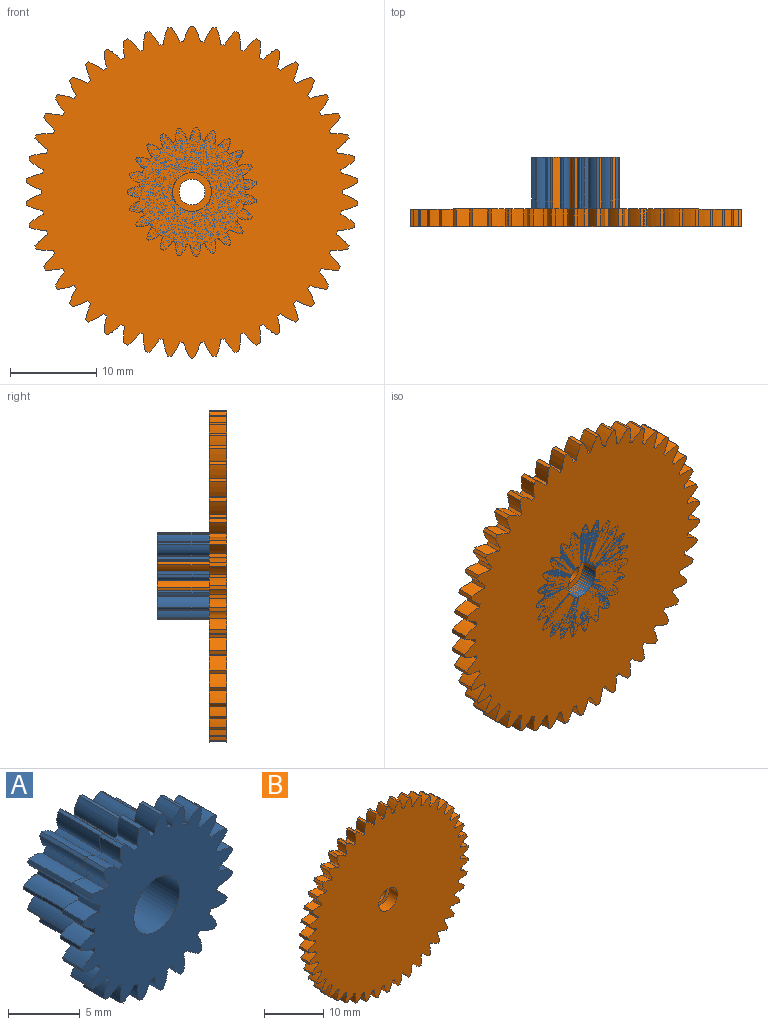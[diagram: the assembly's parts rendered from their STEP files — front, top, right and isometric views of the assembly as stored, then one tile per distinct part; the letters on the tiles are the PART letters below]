
ASSEMBLY  parts=2 mates=1
PART A: 156 faces, bbox 15x8x15 mm
  f0: cylinder r=5.1mm len=6mm, axis (0,-1,0), area 1.7mm2, adj f15,f56,f61,f86
  f1: cylinder r=5.1mm len=6mm, axis (0,-1,0), area 1.7mm2, adj f15,f50,f58,f86
  f2: cylinder r=5.1mm len=6mm, axis (0,-1,0), area 1.7mm2, adj f15,f17,f55,f86
  f3: cylinder r=5.1mm len=6mm, axis (0,-1,0), area 1.7mm2, adj f15,f52,f53,f86
  f4: cylinder r=5.1mm len=6mm, axis (0,-1,0), area 1.7mm2, adj f15,f44,f49,f86
  f5: cylinder r=5.1mm len=6mm, axis (0,-1,0), area 1.7mm2, adj f15,f46,f59,f86
  f6: cylinder r=5.1mm len=6mm, axis (0,-1,0), area 1.7mm2, adj f15,f43,f47,f86
  f7: cylinder r=5.1mm len=6mm, axis (0,-1,0), area 1.7mm2, adj f15,f40,f41,f86
  f8: cylinder r=5.1mm len=6mm, axis (0,-1,0), area 1.7mm2, adj f15,f29,f37,f86
  f9: cylinder r=5.1mm len=6mm, axis (0,-1,0), area 1.7mm2, adj f15,f34,f35,f86
  f10: cylinder r=5.1mm len=6mm, axis (0,-1,0), area 1.7mm2, adj f15,f26,f31,f86
  f11: cylinder r=5.1mm len=6mm, axis (0,-1,0), area 1.7mm2, adj f15,f20,f28,f86
  f12: cylinder r=5.1mm len=6mm, axis (0,-1,0), area 1.7mm2, adj f15,f25,f38,f86
  f13: cylinder r=5.1mm len=6mm, axis (0,-1,0), area 1.7mm2, adj f15,f22,f23,f86
  f14: cylinder r=5.1mm len=6mm, axis (0,-1,0), area 1.7mm2, adj f15,f19,f32,f86
  f15: plane 10.19x10.14mm, normal (0,1,0), area 46mm2, adj f0,f1,f2,f3,f4,f5,f6,f7
  f16: cylinder r=2.25mm len=8mm, axis (0,-1,0), area 113.1mm2, adj f15,f85
  f17: extruded ~6x1.28mm, area 8.8mm2, adj f2,f15,f18,f86
  f18: cylinder r=3.75mm len=6mm, axis (0,-1,0), area 3.4mm2, adj f15,f17,f19,f86
  f19: extruded ~6x1.28mm, area 8.8mm2, adj f14,f15,f18,f86
  f20: extruded ~6x1.43mm, area 8.8mm2, adj f11,f15,f21,f86
  f21: cylinder r=3.75mm len=6mm, axis (0,-1,0), area 3.4mm2, adj f15,f20,f22,f86
  f22: extruded ~6x1.19mm, area 8.8mm2, adj f13,f15,f21,f86
  f23: extruded ~6x1.27mm, area 8.8mm2, adj f13,f15,f24,f86
  f24: cylinder r=3.75mm len=6mm, axis (0,-1,0), area 3.4mm2, adj f15,f23,f25,f86
  f25: extruded ~6x1.41mm, area 8.8mm2, adj f12,f15,f24,f86
  f26: extruded ~6x1.34mm, area 8.8mm2, adj f10,f15,f27,f86
  f27: cylinder r=3.75mm len=6mm, axis (0,-1,0), area 3.4mm2, adj f15,f26,f28,f86
  f28: extruded ~6x1.2mm, area 8.8mm2, adj f11,f15,f27,f86
  f29: extruded ~6x1.02mm, area 8.8mm2, adj f8,f15,f30,f86
  f30: cylinder r=3.75mm len=6mm, axis (0,-1,0), area 3.4mm2, adj f15,f29,f31,f86
  f31: extruded ~6x1.41mm, area 8.8mm2, adj f10,f15,f30,f86
  f32: extruded ~6x1.43mm, area 8.8mm2, adj f14,f15,f33,f86
  f33: cylinder r=3.75mm len=6mm, axis (0,-1,0), area 3.4mm2, adj f15,f32,f34,f86
  f34: extruded ~6x1.1mm, area 8.8mm2, adj f9,f15,f33,f86
  f35: extruded ~6x1.33mm, area 8.8mm2, adj f9,f15,f36,f86
  f36: cylinder r=3.75mm len=6mm, axis (0,-1,0), area 3.4mm2, adj f15,f35,f37,f86
  f37: extruded ~6x1.38mm, area 8.8mm2, adj f8,f15,f36,f86
  f38: extruded ~6x1.12mm, area 8.8mm2, adj f12,f15,f39,f86
  f39: cylinder r=3.75mm len=6mm, axis (0,-1,0), area 3.4mm2, adj f15,f38,f40,f86
  f40: extruded ~6x1.38mm, area 8.8mm2, adj f7,f15,f39,f86
  f41: extruded ~6x1.38mm, area 8.8mm2, adj f7,f15,f42,f86
  f42: cylinder r=3.75mm len=6mm, axis (0,-1,0), area 3.4mm2, adj f15,f41,f43,f86
  f43: extruded ~6x1.12mm, area 8.8mm2, adj f6,f15,f42,f86
  f44: extruded ~6x1.19mm, area 8.8mm2, adj f4,f15,f45,f86
  f45: cylinder r=3.75mm len=6mm, axis (0,-1,0), area 3.4mm2, adj f15,f44,f46,f86
  f46: extruded ~6x1.43mm, area 8.8mm2, adj f5,f15,f45,f86
  f47: extruded ~6x1.41mm, area 8.8mm2, adj f6,f15,f48,f86
  f48: cylinder r=3.75mm len=6mm, axis (0,-1,0), area 3.4mm2, adj f15,f47,f49,f86
  f49: extruded ~6x1.27mm, area 8.8mm2, adj f4,f15,f48,f86
  f50: extruded ~6x1.38mm, area 8.8mm2, adj f1,f15,f51,f86
  f51: cylinder r=3.75mm len=6mm, axis (0,-1,0), area 3.4mm2, adj f15,f50,f52,f86
  f52: extruded ~6x1.33mm, area 8.8mm2, adj f3,f15,f51,f86
  f53: extruded ~6x1.1mm, area 8.8mm2, adj f3,f15,f54,f86
  f54: cylinder r=3.75mm len=6mm, axis (0,-1,0), area 3.4mm2, adj f15,f53,f55,f86
  f55: extruded ~6x1.43mm, area 8.8mm2, adj f2,f15,f54,f86
  f56: extruded ~6x1.41mm, area 8.8mm2, adj f0,f15,f57,f86
  f57: cylinder r=3.75mm len=6mm, axis (0,-1,0), area 3.4mm2, adj f15,f56,f58,f86
  f58: extruded ~6x1.02mm, area 8.8mm2, adj f1,f15,f57,f86
  f59: extruded ~6x1.2mm, area 8.8mm2, adj f5,f15,f60,f86
  f60: cylinder r=3.75mm len=6mm, axis (0,-1,0), area 3.4mm2, adj f15,f59,f61,f86
  f61: extruded ~6x1.34mm, area 8.8mm2, adj f0,f15,f60,f86
  f62: cylinder r=7.5mm len=2mm, axis (0,1,0), area 0.6mm2, adj f85,f86,f150,f155
  f63: cylinder r=7.5mm len=2mm, axis (0,1,0), area 0.6mm2, adj f85,f86,f141,f152
  f64: cylinder r=7.5mm len=2mm, axis (0,1,0), area 0.6mm2, adj f85,f86,f149,f153
  f65: cylinder r=7.5mm len=2mm, axis (0,1,0), area 0.6mm2, adj f85,f86,f146,f147
  f66: cylinder r=7.5mm len=2mm, axis (0,1,0), area 0.6mm2, adj f85,f86,f138,f143
  f67: cylinder r=7.5mm len=2mm, axis (0,1,0), area 0.6mm2, adj f85,f86,f132,f140
  f68: cylinder r=7.5mm len=2mm, axis (0,1,0), area 0.6mm2, adj f85,f86,f129,f137
  f69: cylinder r=7.5mm len=2mm, axis (0,1,0), area 0.6mm2, adj f85,f86,f134,f135
  f70: cylinder r=7.5mm len=2mm, axis (0,1,0), area 0.6mm2, adj f85,f86,f126,f131
  f71: cylinder r=7.5mm len=2mm, axis (0,1,0), area 0.6mm2, adj f85,f86,f123,f128
  f72: cylinder r=7.5mm len=2mm, axis (0,1,0), area 0.6mm2, adj f85,f86,f120,f125
  f73: cylinder r=7.5mm len=2mm, axis (0,1,0), area 0.6mm2, adj f85,f86,f111,f122
  f74: cylinder r=7.5mm len=2mm, axis (0,1,0), area 0.6mm2, adj f85,f86,f87,f119
  f75: cylinder r=7.5mm len=2mm, axis (0,1,0), area 0.6mm2, adj f85,f86,f116,f117
  f76: cylinder r=7.5mm len=2mm, axis (0,1,0), area 0.6mm2, adj f85,f86,f108,f113
  f77: cylinder r=7.5mm len=2mm, axis (0,1,0), area 0.6mm2, adj f85,f86,f110,f114
  f78: cylinder r=7.5mm len=2mm, axis (0,1,0), area 0.6mm2, adj f85,f86,f102,f107
  f79: cylinder r=7.5mm len=2mm, axis (0,1,0), area 0.6mm2, adj f85,f86,f96,f104
  f80: cylinder r=7.5mm len=2mm, axis (0,1,0), area 0.6mm2, adj f85,f86,f93,f101
  f81: cylinder r=7.5mm len=2mm, axis (0,1,0), area 0.6mm2, adj f85,f86,f98,f99
  f82: cylinder r=7.5mm len=2mm, axis (0,1,0), area 0.6mm2, adj f85,f86,f90,f95
  f83: cylinder r=7.5mm len=2mm, axis (0,1,0), area 0.6mm2, adj f85,f86,f92,f144
  f84: cylinder r=7.5mm len=2mm, axis (0,1,0), area 0.6mm2, adj f85,f86,f89,f105
  f85: plane 14.99x14.95mm, normal (0,-1,0), area 131.6mm2, adj f16,f62,f63,f64,f65,f66,f67,f68
  f86: plane 14.99x14.95mm, normal (0,1,0), area 85.7mm2, adj f0,f1,f2,f3,f4,f5,f6,f7
  f87: extruded ~2x1.3mm, area 2.9mm2, adj f74,f85,f86,f88
  f88: cylinder r=6.15mm len=2mm, axis (0,1,0), area 0.9mm2, adj f85,f86,f87,f89
  f89: extruded ~2x1.3mm, area 2.9mm2, adj f84,f85,f86,f88
  f90: extruded ~2x1.34mm, area 2.9mm2, adj f82,f85,f86,f91
  f91: cylinder r=6.15mm len=2mm, axis (0,1,0), area 0.9mm2, adj f85,f86,f90,f92
  f92: extruded ~2x1.26mm, area 2.9mm2, adj f83,f85,f86,f91
  f93: extruded ~2x1.15mm, area 2.9mm2, adj f80,f85,f86,f94
  f94: cylinder r=6.15mm len=2mm, axis (0,1,0), area 0.9mm2, adj f85,f86,f93,f95
  f95: extruded ~2x1.41mm, area 2.9mm2, adj f82,f85,f86,f94
  f96: extruded ~2x1.35mm, area 2.9mm2, adj f79,f85,f86,f97
  f97: cylinder r=6.15mm len=2mm, axis (0,1,0), area 0.9mm2, adj f85,f86,f96,f98
  f98: extruded ~2x1.38mm, area 2.9mm2, adj f81,f85,f86,f97
  f99: extruded ~2x1.16mm, area 2.9mm2, adj f81,f85,f86,f100
  f100: cylinder r=6.15mm len=2mm, axis (0,1,0), area 0.9mm2, adj f85,f86,f99,f101
  f101: extruded ~2x1.45mm, area 2.9mm2, adj f80,f85,f86,f100
  f102: extruded ~2x1.44mm, area 2.9mm2, adj f78,f85,f86,f103
  f103: cylinder r=6.15mm len=2mm, axis (0,1,0), area 0.9mm2, adj f85,f86,f102,f104
  f104: extruded ~2x1.22mm, area 2.9mm2, adj f79,f85,f86,f103
  f105: extruded ~2x1.43mm, area 2.9mm2, adj f84,f85,f86,f106
  f106: cylinder r=6.15mm len=2mm, axis (0,1,0), area 0.9mm2, adj f85,f86,f105,f107
  f107: extruded ~2x1.09mm, area 2.9mm2, adj f78,f85,f86,f106
  f108: extruded ~2x1.38mm, area 2.9mm2, adj f76,f85,f86,f109
  f109: cylinder r=6.15mm len=2mm, axis (0,1,0), area 0.9mm2, adj f85,f86,f108,f110
  f110: extruded ~2x1.35mm, area 2.9mm2, adj f77,f85,f86,f109
  f111: extruded ~2x1.45mm, area 2.9mm2, adj f73,f85,f86,f112
  f112: cylinder r=6.15mm len=2mm, axis (0,1,0), area 0.9mm2, adj f85,f86,f111,f113
  f113: extruded ~2x1.16mm, area 2.9mm2, adj f76,f85,f86,f112
  f114: extruded ~2x1.22mm, area 2.9mm2, adj f77,f85,f86,f115
  f115: cylinder r=6.15mm len=2mm, axis (0,1,0), area 0.9mm2, adj f85,f86,f114,f116
  f116: extruded ~2x1.44mm, area 2.9mm2, adj f75,f85,f86,f115
  f117: extruded ~2x1.09mm, area 2.9mm2, adj f75,f85,f86,f118
  f118: cylinder r=6.15mm len=2mm, axis (0,1,0), area 0.9mm2, adj f85,f86,f117,f119
  f119: extruded ~2x1.43mm, area 2.9mm2, adj f74,f85,f86,f118
  f120: extruded ~2x1.41mm, area 2.9mm2, adj f72,f85,f86,f121
  f121: cylinder r=6.15mm len=2mm, axis (0,1,0), area 0.9mm2, adj f85,f86,f120,f122
  f122: extruded ~2x1.15mm, area 2.9mm2, adj f73,f85,f86,f121
  f123: extruded ~2x1.26mm, area 2.9mm2, adj f71,f85,f86,f124
  f124: cylinder r=6.15mm len=2mm, axis (0,1,0), area 0.9mm2, adj f85,f86,f123,f125
  f125: extruded ~2x1.34mm, area 2.9mm2, adj f72,f85,f86,f124
  f126: extruded ~2x1.03mm, area 2.9mm2, adj f70,f85,f86,f127
  f127: cylinder r=6.15mm len=2mm, axis (0,1,0), area 0.9mm2, adj f85,f86,f126,f128
  f128: extruded ~2x1.44mm, area 2.9mm2, adj f71,f85,f86,f127
  f129: extruded ~2x1.27mm, area 2.9mm2, adj f68,f85,f86,f130
  f130: cylinder r=6.15mm len=2mm, axis (0,1,0), area 0.9mm2, adj f85,f86,f129,f131
  f131: extruded ~2x1.43mm, area 2.9mm2, adj f70,f85,f86,f130
  f132: extruded ~2x1.45mm, area 2.9mm2, adj f67,f85,f86,f133
  f133: cylinder r=6.15mm len=2mm, axis (0,1,0), area 0.9mm2, adj f85,f86,f132,f134
  f134: extruded ~2x1.1mm, area 2.9mm2, adj f69,f85,f86,f133
  f135: extruded ~2x1.41mm, area 2.9mm2, adj f69,f85,f86,f136
  f136: cylinder r=6.15mm len=2mm, axis (0,1,0), area 0.9mm2, adj f85,f86,f135,f137
  f137: extruded ~2x1.31mm, area 2.9mm2, adj f68,f85,f86,f136
  f138: extruded ~2x1.38mm, area 2.9mm2, adj f66,f85,f86,f139
  f139: cylinder r=6.15mm len=2mm, axis (0,1,0), area 0.9mm2, adj f85,f86,f138,f140
  f140: extruded ~2x1.21mm, area 2.9mm2, adj f67,f85,f86,f139
  f141: extruded ~2x1.21mm, area 2.9mm2, adj f63,f85,f86,f142
  f142: cylinder r=6.15mm len=2mm, axis (0,1,0), area 0.9mm2, adj f85,f86,f141,f143
  f143: extruded ~2x1.38mm, area 2.9mm2, adj f66,f85,f86,f142
  f144: extruded ~2x1.44mm, area 2.9mm2, adj f83,f85,f86,f145
  f145: cylinder r=6.15mm len=2mm, axis (0,1,0), area 0.9mm2, adj f85,f86,f144,f146
  f146: extruded ~2x1.03mm, area 2.9mm2, adj f65,f85,f86,f145
  f147: extruded ~2x1.43mm, area 2.9mm2, adj f65,f85,f86,f148
  f148: cylinder r=6.15mm len=2mm, axis (0,1,0), area 0.9mm2, adj f85,f86,f147,f149
  f149: extruded ~2x1.27mm, area 2.9mm2, adj f64,f85,f86,f148
  f150: extruded ~2x1.1mm, area 2.9mm2, adj f62,f85,f86,f151
  f151: cylinder r=6.15mm len=2mm, axis (0,1,0), area 0.9mm2, adj f85,f86,f150,f152
  f152: extruded ~2x1.45mm, area 2.9mm2, adj f63,f85,f86,f151
  f153: extruded ~2x1.31mm, area 2.9mm2, adj f64,f85,f86,f154
  f154: cylinder r=6.15mm len=2mm, axis (0,1,0), area 0.9mm2, adj f85,f86,f153,f155
  f155: extruded ~2x1.41mm, area 2.9mm2, adj f62,f85,f86,f154
PART B: 230 faces, bbox 38.3x8x38.4 mm
  f0: plane 4.5x4.5mm, normal (0,-1,0), area 8.8mm2, adj f12,f89
  f1: cylinder r=4.8mm len=6mm, axis (0,-1,0), area 2mm2, adj f11,f37,f42,f43
  f2: cylinder r=4.8mm len=6mm, axis (0,-1,0), area 2mm2, adj f11,f13,f39,f43
  f3: cylinder r=4.8mm len=6mm, axis (0,-1,0), area 2mm2, adj f11,f31,f36,f43
  f4: cylinder r=4.8mm len=6mm, axis (0,-1,0), area 2mm2, adj f11,f33,f40,f43
  f5: cylinder r=4.8mm len=6mm, axis (0,-1,0), area 2mm2, adj f11,f25,f30,f43
  f6: cylinder r=4.8mm len=6mm, axis (0,-1,0), area 2mm2, adj f11,f22,f27,f43
  f7: cylinder r=4.8mm len=6mm, axis (0,-1,0), area 2mm2, adj f11,f19,f24,f43
  f8: cylinder r=4.8mm len=6mm, axis (0,-1,0), area 2mm2, adj f11,f21,f34,f43
  f9: cylinder r=4.8mm len=6mm, axis (0,-1,0), area 2mm2, adj f11,f18,f28,f43
  f10: cylinder r=4.8mm len=6mm, axis (0,-1,0), area 2mm2, adj f11,f15,f16,f43
  f11: plane 9.64x9.28mm, normal (0,1,0), area 40.8mm2, adj f1,f2,f3,f4,f5,f6,f7,f8
  f12: cylinder r=1.5mm len=6mm, axis (0,-1,0), area 56.5mm2, adj f0,f11
  f13: extruded ~6x1.64mm, area 11.8mm2, adj f2,f11,f14,f43
  f14: cylinder r=3mm len=6mm, axis (0,-1,0), area 4.6mm2, adj f11,f13,f15,f43
  f15: extruded ~6x1.64mm, area 11.8mm2, adj f10,f11,f14,f43
  f16: extruded ~6x1.88mm, area 11.8mm2, adj f10,f11,f17,f43
  f17: cylinder r=3mm len=6mm, axis (0,-1,0), area 4.6mm2, adj f11,f16,f18,f43
  f18: extruded ~6x1.73mm, area 11.8mm2, adj f9,f11,f17,f43
  f19: extruded ~6x1.64mm, area 11.8mm2, adj f7,f11,f20,f43
  f20: cylinder r=3mm len=6mm, axis (0,-1,0), area 4.6mm2, adj f11,f19,f21,f43
  f21: extruded ~6x1.64mm, area 11.8mm2, adj f8,f11,f20,f43
  f22: extruded ~6x1.73mm, area 11.8mm2, adj f6,f11,f23,f43
  f23: cylinder r=3mm len=6mm, axis (0,-1,0), area 4.6mm2, adj f11,f22,f24,f43
  f24: extruded ~6x1.88mm, area 11.8mm2, adj f7,f11,f23,f43
  f25: extruded ~6x1.85mm, area 11.8mm2, adj f5,f11,f26,f43
  f26: cylinder r=3mm len=6mm, axis (0,-1,0), area 4.6mm2, adj f11,f25,f27,f43
  f27: extruded ~6x1.41mm, area 11.8mm2, adj f6,f11,f26,f43
  f28: extruded ~6x1.41mm, area 11.8mm2, adj f9,f11,f29,f43
  f29: cylinder r=3mm len=6mm, axis (0,-1,0), area 4.6mm2, adj f11,f28,f30,f43
  f30: extruded ~6x1.85mm, area 11.8mm2, adj f5,f11,f29,f43
  f31: extruded ~6x1.41mm, area 11.8mm2, adj f3,f11,f32,f43
  f32: cylinder r=3mm len=6mm, axis (0,-1,0), area 4.6mm2, adj f11,f31,f33,f43
  f33: extruded ~6x1.85mm, area 11.8mm2, adj f4,f11,f32,f43
  f34: extruded ~6x1.88mm, area 11.8mm2, adj f8,f11,f35,f43
  f35: cylinder r=3mm len=6mm, axis (0,-1,0), area 4.6mm2, adj f11,f34,f36,f43
  f36: extruded ~6x1.73mm, area 11.8mm2, adj f3,f11,f35,f43
  f37: extruded ~6x1.73mm, area 11.8mm2, adj f1,f11,f38,f43
  f38: cylinder r=3mm len=6mm, axis (0,-1,0), area 4.6mm2, adj f11,f37,f39,f43
  f39: extruded ~6x1.88mm, area 11.8mm2, adj f2,f11,f38,f43
  f40: extruded ~6x1.85mm, area 11.8mm2, adj f4,f11,f41,f43
  f41: cylinder r=3mm len=6mm, axis (0,-1,0), area 4.6mm2, adj f11,f40,f42,f43
  f42: extruded ~6x1.41mm, area 11.8mm2, adj f1,f11,f41,f43
  f43: plane 38.4x38.34mm, normal (0,1,0), area 1010.5mm2, adj f1,f2,f3,f4,f5,f6,f7,f8
  f44: cylinder r=19.2mm len=2mm, axis (0,1,0), area 0.9mm2, adj f43,f91,f203,f229
  f45: cylinder r=19.2mm len=2mm, axis (0,1,0), area 0.9mm2, adj f43,f91,f226,f227
  f46: cylinder r=19.2mm len=2mm, axis (0,1,0), area 0.9mm2, adj f43,f91,f218,f223
  f47: cylinder r=19.2mm len=2mm, axis (0,1,0), area 0.9mm2, adj f43,f91,f220,f224
  f48: cylinder r=19.2mm len=2mm, axis (0,1,0), area 0.9mm2, adj f43,f91,f212,f217
  f49: cylinder r=19.2mm len=2mm, axis (0,1,0), area 0.9mm2, adj f43,f91,f214,f221
  f50: cylinder r=19.2mm len=2mm, axis (0,1,0), area 0.9mm2, adj f43,f91,f211,f215
  f51: cylinder r=19.2mm len=2mm, axis (0,1,0), area 0.9mm2, adj f43,f91,f208,f209
  f52: cylinder r=19.2mm len=2mm, axis (0,1,0), area 0.9mm2, adj f43,f91,f200,f205
  f53: cylinder r=19.2mm len=2mm, axis (0,1,0), area 0.9mm2, adj f43,f91,f197,f202
  f54: cylinder r=19.2mm len=2mm, axis (0,1,0), area 0.9mm2, adj f43,f91,f194,f199
  f55: cylinder r=19.2mm len=2mm, axis (0,1,0), area 0.9mm2, adj f43,f91,f182,f196
  f56: cylinder r=19.2mm len=2mm, axis (0,1,0), area 0.9mm2, adj f43,f91,f188,f193
  f57: cylinder r=19.2mm len=2mm, axis (0,1,0), area 0.9mm2, adj f43,f91,f179,f190
  f58: cylinder r=19.2mm len=2mm, axis (0,1,0), area 0.9mm2, adj f43,f91,f187,f191
  f59: cylinder r=19.2mm len=2mm, axis (0,1,0), area 0.9mm2, adj f43,f91,f184,f185
  f60: cylinder r=19.2mm len=2mm, axis (0,1,0), area 0.9mm2, adj f43,f91,f176,f181
  f61: cylinder r=19.2mm len=2mm, axis (0,1,0), area 0.9mm2, adj f43,f91,f173,f178
  f62: cylinder r=19.2mm len=2mm, axis (0,1,0), area 0.9mm2, adj f43,f91,f170,f175
  f63: cylinder r=19.2mm len=2mm, axis (0,1,0), area 0.9mm2, adj f43,f91,f167,f172
  f64: cylinder r=19.2mm len=2mm, axis (0,1,0), area 0.9mm2, adj f43,f91,f164,f169
  f65: cylinder r=19.2mm len=2mm, axis (0,1,0), area 0.9mm2, adj f43,f91,f161,f166
  f66: cylinder r=19.2mm len=2mm, axis (0,1,0), area 0.9mm2, adj f43,f91,f158,f163
  f67: cylinder r=19.2mm len=2mm, axis (0,1,0), area 0.9mm2, adj f43,f91,f143,f160
  f68: cylinder r=19.2mm len=2mm, axis (0,1,0), area 0.9mm2, adj f43,f91,f92,f157
  f69: cylinder r=19.2mm len=2mm, axis (0,1,0), area 0.9mm2, adj f43,f91,f154,f155
  f70: cylinder r=19.2mm len=2mm, axis (0,1,0), area 0.9mm2, adj f43,f91,f151,f152
  f71: cylinder r=19.2mm len=2mm, axis (0,1,0), area 0.9mm2, adj f43,f91,f148,f149
  f72: cylinder r=19.2mm len=2mm, axis (0,1,0), area 0.9mm2, adj f43,f91,f140,f145
  f73: cylinder r=19.2mm len=2mm, axis (0,1,0), area 0.9mm2, adj f43,f91,f134,f142
  f74: cylinder r=19.2mm len=2mm, axis (0,1,0), area 0.9mm2, adj f43,f91,f139,f146
  f75: cylinder r=19.2mm len=2mm, axis (0,1,0), area 0.9mm2, adj f43,f91,f136,f137
  f76: cylinder r=19.2mm len=2mm, axis (0,1,0), area 0.9mm2, adj f43,f91,f128,f133
  f77: cylinder r=19.2mm len=2mm, axis (0,1,0), area 0.9mm2, adj f43,f91,f125,f130
  f78: cylinder r=19.2mm len=2mm, axis (0,1,0), area 0.9mm2, adj f43,f91,f119,f127
  f79: cylinder r=19.2mm len=2mm, axis (0,1,0), area 0.9mm2, adj f43,f91,f113,f124
  f80: cylinder r=19.2mm len=2mm, axis (0,1,0), area 0.9mm2, adj f43,f91,f121,f122
  f81: cylinder r=19.2mm len=2mm, axis (0,1,0), area 0.9mm2, adj f43,f91,f110,f118
  f82: cylinder r=19.2mm len=2mm, axis (0,1,0), area 0.9mm2, adj f43,f91,f115,f116
  f83: cylinder r=19.2mm len=2mm, axis (0,1,0), area 0.9mm2, adj f43,f91,f107,f112
  f84: cylinder r=19.2mm len=2mm, axis (0,1,0), area 0.9mm2, adj f43,f91,f104,f109
  f85: cylinder r=19.2mm len=2mm, axis (0,1,0), area 0.9mm2, adj f43,f91,f101,f106
  f86: cylinder r=19.2mm len=2mm, axis (0,1,0), area 0.9mm2, adj f43,f91,f98,f103
  f87: cylinder r=19.2mm len=2mm, axis (0,1,0), area 0.9mm2, adj f43,f91,f95,f100
  f88: cylinder r=19.2mm len=2mm, axis (0,1,0), area 0.9mm2, adj f43,f91,f97,f206
  f89: cylinder r=2.25mm len=4.5mm, axis (0,1,0), area 28.3mm2, adj f0,f91
  f90: cylinder r=19.2mm len=2mm, axis (0,1,0), area 0.9mm2, adj f43,f91,f94,f131
  f91: plane 38.4x38.34mm, normal (0,-1,0), area 1042.5mm2, adj f44,f45,f46,f47,f48,f49,f50,f51
  f92: extruded ~2x1.77mm, area 4mm2, adj f43,f68,f91,f93
  f93: cylinder r=17.4mm len=2mm, axis (0,1,0), area 0.9mm2, adj f43,f91,f92,f94
  f94: extruded ~2x1.77mm, area 4mm2, adj f43,f90,f91,f93
  f95: extruded ~2x1.91mm, area 4mm2, adj f43,f87,f91,f96
  f96: cylinder r=17.4mm len=2mm, axis (0,1,0), area 0.9mm2, adj f43,f91,f95,f97
  f97: extruded ~2x1.56mm, area 4mm2, adj f43,f88,f91,f96
  f98: extruded ~2x1.83mm, area 4mm2, adj f43,f86,f91,f99
  f99: cylinder r=17.4mm len=2mm, axis (0,1,0), area 0.9mm2, adj f43,f91,f98,f100
  f100: extruded ~2x1.71mm, area 4mm2, adj f43,f87,f91,f99
  f101: extruded ~2x1.71mm, area 4mm2, adj f43,f85,f91,f102
  f102: cylinder r=17.4mm len=2mm, axis (0,1,0), area 0.9mm2, adj f43,f91,f101,f103
  f103: extruded ~2x1.83mm, area 4mm2, adj f43,f86,f91,f102
  f104: extruded ~2x1.56mm, area 4mm2, adj f43,f84,f91,f105
  f105: cylinder r=17.4mm len=2mm, axis (0,1,0), area 0.9mm2, adj f43,f91,f104,f106
  f106: extruded ~2x1.91mm, area 4mm2, adj f43,f85,f91,f105
  f107: extruded ~2x1.41mm, area 4mm2, adj f43,f83,f91,f108
  f108: cylinder r=17.4mm len=2mm, axis (0,1,0), area 0.9mm2, adj f43,f91,f107,f109
  f109: extruded ~2x1.96mm, area 4mm2, adj f43,f84,f91,f108
  f110: extruded ~2x1.58mm, area 4mm2, adj f43,f81,f91,f111
  f111: cylinder r=17.4mm len=2mm, axis (0,1,0), area 0.9mm2, adj f43,f91,f110,f112
  f112: extruded ~2x1.97mm, area 4mm2, adj f43,f83,f91,f111
  f113: extruded ~2x1.84mm, area 4mm2, adj f43,f79,f91,f114
  f114: cylinder r=17.4mm len=2mm, axis (0,1,0), area 0.9mm2, adj f43,f91,f113,f115
  f115: extruded ~2x1.88mm, area 4mm2, adj f43,f82,f91,f114
  f116: extruded ~2x1.73mm, area 4mm2, adj f43,f82,f91,f117
  f117: cylinder r=17.4mm len=2mm, axis (0,1,0), area 0.9mm2, adj f43,f91,f116,f118
  f118: extruded ~2x1.94mm, area 4mm2, adj f43,f81,f91,f117
  f119: extruded ~2x1.96mm, area 4mm2, adj f43,f78,f91,f120
  f120: cylinder r=17.4mm len=2mm, axis (0,1,0), area 0.9mm2, adj f43,f91,f119,f121
  f121: extruded ~2x1.66mm, area 4mm2, adj f43,f80,f91,f120
  f122: extruded ~2x1.92mm, area 4mm2, adj f43,f80,f91,f123
  f123: cylinder r=17.4mm len=2mm, axis (0,1,0), area 0.9mm2, adj f43,f91,f122,f124
  f124: extruded ~2x1.79mm, area 4mm2, adj f43,f79,f91,f123
  f125: extruded ~2x1.97mm, area 4mm2, adj f43,f77,f91,f126
  f126: cylinder r=17.4mm len=2mm, axis (0,1,0), area 0.9mm2, adj f43,f91,f125,f127
  f127: extruded ~2x1.5mm, area 4mm2, adj f43,f78,f91,f126
  f128: extruded ~2x1.94mm, area 4mm2, adj f43,f76,f91,f129
  f129: cylinder r=17.4mm len=2mm, axis (0,1,0), area 0.9mm2, adj f43,f91,f128,f130
  f130: extruded ~2x1.47mm, area 4mm2, adj f43,f77,f91,f129
  f131: extruded ~2x1.87mm, area 4mm2, adj f43,f90,f91,f132
  f132: cylinder r=17.4mm len=2mm, axis (0,1,0), area 0.9mm2, adj f43,f91,f131,f133
  f133: extruded ~2x1.64mm, area 4mm2, adj f43,f76,f91,f132
  f134: extruded ~2x1.88mm, area 4mm2, adj f43,f73,f91,f135
  f135: cylinder r=17.4mm len=2mm, axis (0,1,0), area 0.9mm2, adj f43,f91,f134,f136
  f136: extruded ~2x1.84mm, area 4mm2, adj f43,f75,f91,f135
  f137: extruded ~2x1.79mm, area 4mm2, adj f43,f75,f91,f138
  f138: cylinder r=17.4mm len=2mm, axis (0,1,0), area 0.9mm2, adj f43,f91,f137,f139
  f139: extruded ~2x1.92mm, area 4mm2, adj f43,f74,f91,f138
  f140: extruded ~2x1.94mm, area 4mm2, adj f43,f72,f91,f141
  f141: cylinder r=17.4mm len=2mm, axis (0,1,0), area 0.9mm2, adj f43,f91,f140,f142
  f142: extruded ~2x1.73mm, area 4mm2, adj f43,f73,f91,f141
  f143: extruded ~2x1.97mm, area 4mm2, adj f43,f67,f91,f144
  f144: cylinder r=17.4mm len=2mm, axis (0,1,0), area 0.9mm2, adj f43,f91,f143,f145
  f145: extruded ~2x1.58mm, area 4mm2, adj f43,f72,f91,f144
  f146: extruded ~2x1.66mm, area 4mm2, adj f43,f74,f91,f147
  f147: cylinder r=17.4mm len=2mm, axis (0,1,0), area 0.9mm2, adj f43,f91,f146,f148
  f148: extruded ~2x1.96mm, area 4mm2, adj f43,f71,f91,f147
  f149: extruded ~2x1.5mm, area 4mm2, adj f43,f71,f91,f150
  f150: cylinder r=17.4mm len=2mm, axis (0,1,0), area 0.9mm2, adj f43,f91,f149,f151
  f151: extruded ~2x1.97mm, area 4mm2, adj f43,f70,f91,f150
  f152: extruded ~2x1.47mm, area 4mm2, adj f43,f70,f91,f153
  f153: cylinder r=17.4mm len=2mm, axis (0,1,0), area 0.9mm2, adj f43,f91,f152,f154
  f154: extruded ~2x1.94mm, area 4mm2, adj f43,f69,f91,f153
  f155: extruded ~2x1.64mm, area 4mm2, adj f43,f69,f91,f156
  f156: cylinder r=17.4mm len=2mm, axis (0,1,0), area 0.9mm2, adj f43,f91,f155,f157
  f157: extruded ~2x1.87mm, area 4mm2, adj f43,f68,f91,f156
  f158: extruded ~2x1.96mm, area 4mm2, adj f43,f66,f91,f159
  f159: cylinder r=17.4mm len=2mm, axis (0,1,0), area 0.9mm2, adj f43,f91,f158,f160
  f160: extruded ~2x1.41mm, area 4mm2, adj f43,f67,f91,f159
  f161: extruded ~2x1.91mm, area 4mm2, adj f43,f65,f91,f162
  f162: cylinder r=17.4mm len=2mm, axis (0,1,0), area 0.9mm2, adj f43,f91,f161,f163
  f163: extruded ~2x1.56mm, area 4mm2, adj f43,f66,f91,f162
  f164: extruded ~2x1.83mm, area 4mm2, adj f43,f64,f91,f165
  f165: cylinder r=17.4mm len=2mm, axis (0,1,0), area 0.9mm2, adj f43,f91,f164,f166
  f166: extruded ~2x1.71mm, area 4mm2, adj f43,f65,f91,f165
  f167: extruded ~2x1.71mm, area 4mm2, adj f43,f63,f91,f168
  f168: cylinder r=17.4mm len=2mm, axis (0,1,0), area 0.9mm2, adj f43,f91,f167,f169
  f169: extruded ~2x1.83mm, area 4mm2, adj f43,f64,f91,f168
  f170: extruded ~2x1.56mm, area 4mm2, adj f43,f62,f91,f171
  f171: cylinder r=17.4mm len=2mm, axis (0,1,0), area 0.9mm2, adj f43,f91,f170,f172
  f172: extruded ~2x1.91mm, area 4mm2, adj f43,f63,f91,f171
  f173: extruded ~2x1.41mm, area 4mm2, adj f43,f61,f91,f174
  f174: cylinder r=17.4mm len=2mm, axis (0,1,0), area 0.9mm2, adj f43,f91,f173,f175
  f175: extruded ~2x1.96mm, area 4mm2, adj f43,f62,f91,f174
  f176: extruded ~2x1.58mm, area 4mm2, adj f43,f60,f91,f177
  f177: cylinder r=17.4mm len=2mm, axis (0,1,0), area 0.9mm2, adj f43,f91,f176,f178
  f178: extruded ~2x1.97mm, area 4mm2, adj f43,f61,f91,f177
  f179: extruded ~2x1.73mm, area 4mm2, adj f43,f57,f91,f180
  f180: cylinder r=17.4mm len=2mm, axis (0,1,0), area 0.9mm2, adj f43,f91,f179,f181
  f181: extruded ~2x1.94mm, area 4mm2, adj f43,f60,f91,f180
  f182: extruded ~2x1.97mm, area 4mm2, adj f43,f55,f91,f183
  f183: cylinder r=17.4mm len=2mm, axis (0,1,0), area 0.9mm2, adj f43,f91,f182,f184
  f184: extruded ~2x1.5mm, area 4mm2, adj f43,f59,f91,f183
  f185: extruded ~2x1.96mm, area 4mm2, adj f43,f59,f91,f186
  f186: cylinder r=17.4mm len=2mm, axis (0,1,0), area 0.9mm2, adj f43,f91,f185,f187
  f187: extruded ~2x1.66mm, area 4mm2, adj f43,f58,f91,f186
  f188: extruded ~2x1.84mm, area 4mm2, adj f43,f56,f91,f189
  f189: cylinder r=17.4mm len=2mm, axis (0,1,0), area 0.9mm2, adj f43,f91,f188,f190
  f190: extruded ~2x1.88mm, area 4mm2, adj f43,f57,f91,f189
  f191: extruded ~2x1.92mm, area 4mm2, adj f43,f58,f91,f192
  f192: cylinder r=17.4mm len=2mm, axis (0,1,0), area 0.9mm2, adj f43,f91,f191,f193
  f193: extruded ~2x1.79mm, area 4mm2, adj f43,f56,f91,f192
  f194: extruded ~2x1.94mm, area 4mm2, adj f43,f54,f91,f195
  f195: cylinder r=17.4mm len=2mm, axis (0,1,0), area 0.9mm2, adj f43,f91,f194,f196
  f196: extruded ~2x1.47mm, area 4mm2, adj f43,f55,f91,f195
  f197: extruded ~2x1.87mm, area 4mm2, adj f43,f53,f91,f198
  f198: cylinder r=17.4mm len=2mm, axis (0,1,0), area 0.9mm2, adj f43,f91,f197,f199
  f199: extruded ~2x1.64mm, area 4mm2, adj f43,f54,f91,f198
  f200: extruded ~2x1.77mm, area 4mm2, adj f43,f52,f91,f201
  f201: cylinder r=17.4mm len=2mm, axis (0,1,0), area 0.9mm2, adj f43,f91,f200,f202
  f202: extruded ~2x1.77mm, area 4mm2, adj f43,f53,f91,f201
  f203: extruded ~2x1.64mm, area 4mm2, adj f43,f44,f91,f204
  f204: cylinder r=17.4mm len=2mm, axis (0,1,0), area 0.9mm2, adj f43,f91,f203,f205
  f205: extruded ~2x1.87mm, area 4mm2, adj f43,f52,f91,f204
  f206: extruded ~2x1.96mm, area 4mm2, adj f43,f88,f91,f207
  f207: cylinder r=17.4mm len=2mm, axis (0,1,0), area 0.9mm2, adj f43,f91,f206,f208
  f208: extruded ~2x1.41mm, area 4mm2, adj f43,f51,f91,f207
  f209: extruded ~2x1.97mm, area 4mm2, adj f43,f51,f91,f210
  f210: cylinder r=17.4mm len=2mm, axis (0,1,0), area 0.9mm2, adj f43,f91,f209,f211
  f211: extruded ~2x1.58mm, area 4mm2, adj f43,f50,f91,f210
  f212: extruded ~2x1.88mm, area 4mm2, adj f43,f48,f91,f213
  f213: cylinder r=17.4mm len=2mm, axis (0,1,0), area 0.9mm2, adj f43,f91,f212,f214
  f214: extruded ~2x1.84mm, area 4mm2, adj f43,f49,f91,f213
  f215: extruded ~2x1.94mm, area 4mm2, adj f43,f50,f91,f216
  f216: cylinder r=17.4mm len=2mm, axis (0,1,0), area 0.9mm2, adj f43,f91,f215,f217
  f217: extruded ~2x1.73mm, area 4mm2, adj f43,f48,f91,f216
  f218: extruded ~2x1.66mm, area 4mm2, adj f43,f46,f91,f219
  f219: cylinder r=17.4mm len=2mm, axis (0,1,0), area 0.9mm2, adj f43,f91,f218,f220
  f220: extruded ~2x1.96mm, area 4mm2, adj f43,f47,f91,f219
  f221: extruded ~2x1.79mm, area 4mm2, adj f43,f49,f91,f222
  f222: cylinder r=17.4mm len=2mm, axis (0,1,0), area 0.9mm2, adj f43,f91,f221,f223
  f223: extruded ~2x1.92mm, area 4mm2, adj f43,f46,f91,f222
  f224: extruded ~2x1.5mm, area 4mm2, adj f43,f47,f91,f225
  f225: cylinder r=17.4mm len=2mm, axis (0,1,0), area 0.9mm2, adj f43,f91,f224,f226
  f226: extruded ~2x1.97mm, area 4mm2, adj f43,f45,f91,f225
  f227: extruded ~2x1.47mm, area 4mm2, adj f43,f45,f91,f228
  f228: cylinder r=17.4mm len=2mm, axis (0,1,0), area 0.9mm2, adj f43,f91,f227,f229
  f229: extruded ~2x1.94mm, area 4mm2, adj f43,f44,f91,f228
PLACE A t=(2.19,-1.99,-0.53)mm
PLACE B t=(2.19,-1.99,-0.53)mm
MATE fastened A.f0 <-> B.f1  axis (0,-1,0) through (2.19,-3.99,-0.53)mm
